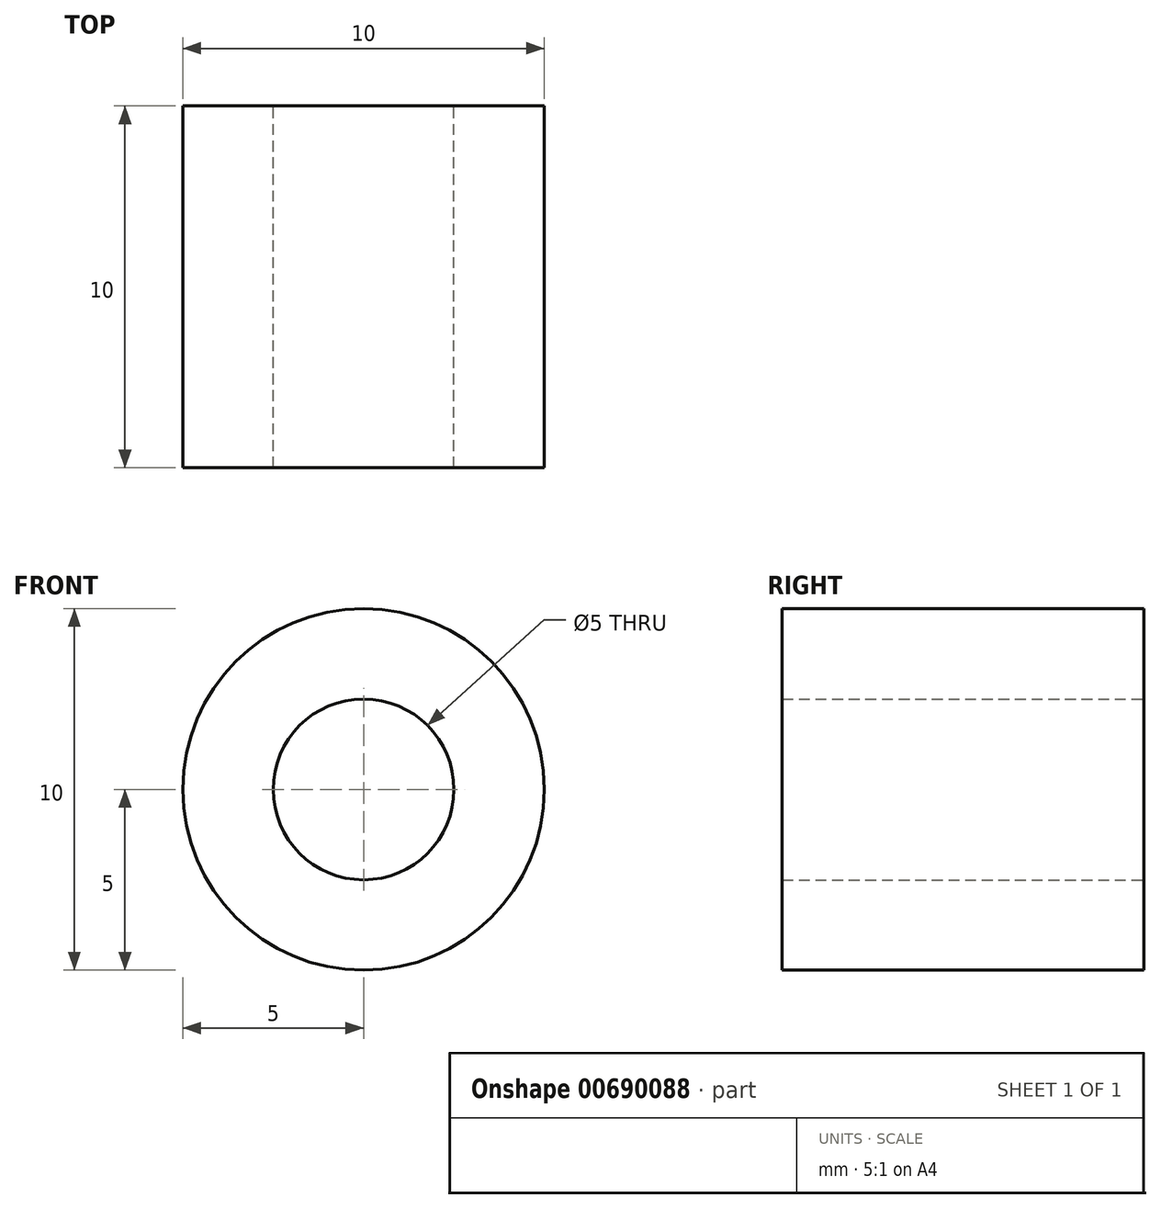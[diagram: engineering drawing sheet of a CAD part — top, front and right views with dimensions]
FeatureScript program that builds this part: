
annotation { "Feature Type Name" : "Feature", "Feature Type Description" : "" }
export const myFeature = defineFeature(function(context is Context, id is Id, definition is map)
    precondition{}
    {
        {
            var Q0;
            Q0=qCreatedBy(makeId("Front.planeOp"),FACE);
            var sketch = newSketch(context, id + "F0", { "sketchPlane" : qUnion([Q0])});
            skCircle(sketch, "E0", {"center": v(0, 0) * mm, "radius": 5 * mm});
            skCircle(sketch, "E1", {"center": v(0, 0) * mm, "radius": 2.5 * mm});
            skSolve(sketch);
        }
        {
            var Q0;
            Q0=makeQuery(id+"F0.imprint","IMPRINT",FACE,{"disambiguationData":[TD([[makeQuery(id+"F0.imprint","IMPRINT",EDGE,{"derivedFrom":sQuery(id+"F0.wireOp",EDGE,"E0")}),1.0]])]});
            extrude(context, id + "F1", {"entities" : qUnion([Q0]), "depth" : 10 * mm, "offsetDistance" : 25 * mm});
        }
    });
